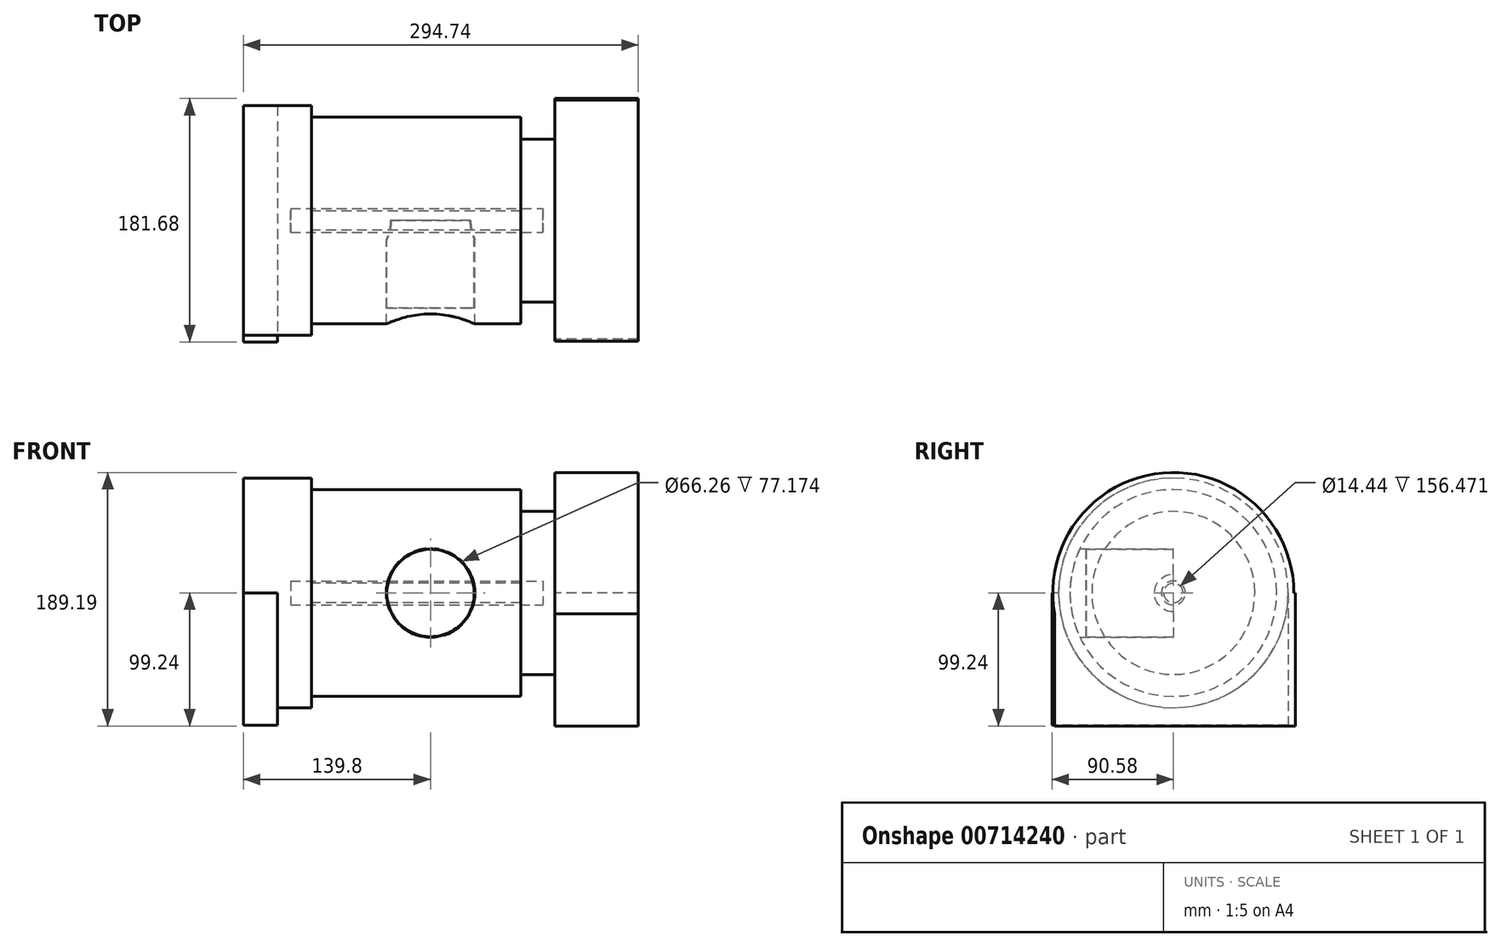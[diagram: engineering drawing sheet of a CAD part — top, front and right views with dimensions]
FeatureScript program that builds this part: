
annotation { "Feature Type Name" : "Feature", "Feature Type Description" : "" }
export const myFeature = defineFeature(function(context is Context, id is Id, definition is map)
    precondition{}
    {
        {
            var Q0;
            Q0=qCreatedBy(makeId("Front.planeOp"),FACE);
            var sketch = newSketch(context, id + "F0", { "sketchPlane" : qUnion([Q0])});
            skLineSegment(sketch, "E0.bottom", {"start": v(76.5, -43.24) * mm, "end": v(-76.5, -43.24) * mm});
            skLineSegment(sketch, "E0.top", {"start": v(76.5, 43.24) * mm, "end": v(-76.5, 43.24) * mm});
            skLineSegment(sketch, "E0.left", {"start": v(76.5, -43.24) * mm, "end": v(76.5, 43.24) * mm});
            skLineSegment(sketch, "E0.right", {"start": v(-76.5, -43.24) * mm, "end": v(-76.5, 43.24) * mm});
            skPoint(sketch, "E0.middle", {"position": v(0, 0) * mm});
            skSolve(sketch);
        }
        {
            var Q0;
            Q0=qCreatedBy(makeId("Right.planeOp"),FACE);
            var sketch = newSketch(context, id + "F1", { "sketchPlane" : qUnion([Q0])});
            skCircle(sketch, "E1", {"center": v(0, 0) * mm, "radius": 77.17 * mm});
            skSolve(sketch);
        }
        {
            var Q0;
            Q0=makeQuery(id+"F1.imprint","IMPRINT",FACE,{"disambiguationData":[TD([[makeQuery(id+"F1.imprint","IMPRINT",EDGE,{"derivedFrom":sQuery(id+"F1.wireOp",EDGE,"E1")}),1.0]])]});
            extrude(context, id + "F2", {"entities" : qUnion([Q0]), "oppositeDirection" : true, "depth" : 63.6 * mm, "offsetDistance" : 25.4 * mm, "hasSecondDirection" : true, "secondDirectionOppositeDirection" : false, "secondDirectionDepth" : 71.9 * mm});
        }
        {
            var Q0;
            Q0=makeQuery(id+"F2.opExtrude","CAP_FACE",FACE,{"disambiguationData":[OSD([sQuery(id+"F1.wireOp",EDGE,"E1")])],"isStart":true});
            var sketch = newSketch(context, id + "F3", { "sketchPlane" : qUnion([Q0])});
            skSolve(sketch);
        }
        {
            var Q0;
            Q0=makeQuery(id+"F3.imprint","IMPRINT",FACE,{"disambiguationData":[TD([[makeQuery(id+"F3.imprint","IMPRINT",EDGE,{"derivedFrom":makeQuery(id+"F2.opExtrude","CAP_EDGE",EDGE,{"disambiguationData":[OSD([sQuery(id+"F1.wireOp",EDGE,"E1")])],"isStart":true})}),1.0]])]});
            extrude(context, id + "F4", {"entities" : qUnion([Q0]), "operationType" : NewBodyOperationType.REMOVE, "oppositeDirection" : true, "depth" : 4.44 * mm, "offsetDistance" : 25.4 * mm});
        }
        {
            var Q0;
            Q0 = qSketchRegion(id + "F0", true);
            var sketch = newSketch(context, id + "F5", { "sketchPlane" : qUnion([Q0])});
            skCircle(sketch, "E2", {"center": v(0, 0) * mm, "radius": 33.13 * mm});
            skSolve(sketch);
        }
        {
            var Q0;
            Q0 = qSketchRegion(id + "F5", true);
            extrude(context, id + "F6", {"entities" : qUnion([Q0]), "operationType" : NewBodyOperationType.REMOVE, "depth" : 189.18 * mm, "offsetDistance" : 25.4 * mm});
        }
        {
            var Q0;
            Q0=makeQuery(id+"F0.imprint","IMPRINT",FACE,{"disambiguationData":[TD([[makeQuery(id+"F0.imprint","IMPRINT",EDGE,{"derivedFrom":sQuery(id+"F0.wireOp",EDGE,"E0.bottom")}),-1.0]])]});
            var sketch = newSketch(context, id + "F7", { "sketchPlane" : qUnion([Q0])});
            skCircle(sketch, "E3", {"center": v(0, 0) * mm, "radius": 32.56 * mm});
            skSolve(sketch);
        }
        {
            var Q0;
            Q0 = qSketchRegion(id + "F7", true);
            extrude(context, id + "F8", {"entities" : qUnion([Q0]), "depth" : 65.27 * mm, "offsetDistance" : 25.4 * mm});
        }
        {
            var Q0;
            Q0=makeQuery(id+"F2.opExtrude","CAP_FACE",FACE,{"disambiguationData":[OSD([sQuery(id+"F1.wireOp",EDGE,"E1")])],"isStart":false});
            var sketch = newSketch(context, id + "F9", { "sketchPlane" : qUnion([Q0])});
            skCircle(sketch, "E4", {"center": v(0, 0) * mm, "radius": 7.22 * mm});
            skSolve(sketch);
        }
        {
            var Q0;
            Q0=makeQuery(id+"F9.imprint","IMPRINT",FACE,{"disambiguationData":[TD([[makeQuery(id+"F9.imprint","IMPRINT",EDGE,{"derivedFrom":sQuery(id+"F9.wireOp",EDGE,"E4")}),1.0]])]});
            extrude(context, id + "F10", {"entities" : qUnion([Q0]), "operationType" : NewBodyOperationType.REMOVE, "oppositeDirection" : true, "depth" : 260.35 * mm, "offsetDistance" : 25.4 * mm});
        }
        {
            var Q0;
            Q0=makeQuery(id+"F2.opExtrude","CAP_FACE",FACE,{"disambiguationData":[OSD([sQuery(id+"F1.wireOp",EDGE,"E1")])],"isStart":false});
            var sketch = newSketch(context, id + "F11", { "sketchPlane" : qUnion([Q0])});
            skCircle(sketch, "E5", {"center": v(0, 0) * mm, "radius": 6.55 * mm});
            skSolve(sketch);
        }
        {
            var Q0;
            Q0=makeQuery(id+"F11.imprint","IMPRINT",FACE,{"disambiguationData":[TD([[makeQuery(id+"F11.imprint","IMPRINT",EDGE,{"derivedFrom":sQuery(id+"F11.wireOp",EDGE,"E5")}),-1.0]])]});
            extrude(context, id + "F12", {"entities" : qUnion([Q0]), "operationType" : NewBodyOperationType.REMOVE, "oppositeDirection" : true, "depth" : 115.25 * mm, "offsetDistance" : 25.4 * mm});
        }
        {
            var Q0;
            Q0=makeQuery(id+"F2.opExtrude","CAP_FACE",FACE,{"disambiguationData":[OSD([sQuery(id+"F1.wireOp",EDGE,"E1")])],"isStart":false});
            var sketch = newSketch(context, id + "F13", { "sketchPlane" : qUnion([Q0])});
            skCircle(sketch, "E6", {"center": v(0, 0) * mm, "radius": 14.1 * mm});
            skSolve(sketch);
        }
        {
            var Q0;
            Q0=makeQuery(id+"F13.imprint","IMPRINT",FACE,{"disambiguationData":[TD([[makeQuery(id+"F13.imprint","IMPRINT",EDGE,{"derivedFrom":sQuery(id+"F13.wireOp",EDGE,"E6")}),1.0]])]});
            extrude(context, id + "F14", {"entities" : qUnion([Q0]), "operationType" : NewBodyOperationType.ADD, "oppositeDirection" : true, "depth" : 172.6 * mm, "offsetDistance" : 25.4 * mm});
        }
        {
            var Q0;
            Q0=makeQuery(id+"F2.opExtrude","CAP_FACE",FACE,{"disambiguationData":[OSD([sQuery(id+"F1.wireOp",EDGE,"E1")])],"isStart":false});
            extrude(context, id + "F15", {"entities" : qUnion([Q0]), "operationType" : NewBodyOperationType.ADD, "depth" : 25.4 * mm, "offsetDistance" : 25.4 * mm});
        }
        {
            var Q0;
            Q0=makeQuery(id+"F15.opExtrude","CAP_FACE",FACE,{"disambiguationData":[OSD([sQuery(id+"F1.wireOp",EDGE,"E1")])],"isStart":false});
            var sketch = newSketch(context, id + "F16", { "sketchPlane" : qUnion([Q0])});
            skCircle(sketch, "E7", {"center": v(0, 0) * mm, "radius": 8.91 * mm});
            skSolve(sketch);
        }
        {
            var Q0;
            Q0 = qSketchRegion(id + "F16", true);
            extrude(context, id + "F17", {"entities" : qUnion([Q0]), "depth" : 15.58 * mm, "offsetDistance" : 25.4 * mm, "hasSecondDirection" : true, "secondDirectionOppositeDirection" : true, "secondDirectionDepth" : 172.93 * mm});
        }
        {
            var Q0;
            Q0=makeQuery(id+"F4.boolean.opBoolean","COPY",FACE,{"derivedFrom":makeQuery(id+"F4.opExtrude","CAP_FACE",FACE,{"disambiguationData":[OSD([sQuery(id+"F1.wireOp",EDGE,"E1")])],"isStart":false})});
            var sketch = newSketch(context, id + "F18", { "sketchPlane" : qUnion([Q0])});
            skCircle(sketch, "E8", {"center": v(0, 0) * mm, "radius": 60.82 * mm});
            skSolve(sketch);
        }
        {
            var Q0;
            Q0 = qSketchRegion(id + "F18", true);
            extrude(context, id + "F19", {"entities" : qUnion([Q0]), "depth" : 25.4 * mm, "offsetDistance" : 25.4 * mm});
        }
        {
            var Q0;
            Q0=makeQuery(id+"F15.opExtrude","CAP_FACE",FACE,{"disambiguationData":[OSD([sQuery(id+"F1.wireOp",EDGE,"E1")])],"isStart":false});
            var sketch = newSketch(context, id + "F20", { "sketchPlane" : qUnion([Q0])});
            skCircle(sketch, "E9", {"center": v(0, 0) * mm, "radius": 85.72 * mm});
            skSolve(sketch);
        }
        {
            var Q0;
            Q0 = qSketchRegion(id + "F20", true);
            extrude(context, id + "F21", {"entities" : qUnion([Q0]), "depth" : 25.4 * mm, "offsetDistance" : 25.4 * mm});
        }
        {
            var Q0;
            Q0=makeQuery(id+"F19.opExtrude","CAP_FACE",FACE,{"disambiguationData":[OSD([sQuery(id+"F18.wireOp",EDGE,"E8")])],"isStart":false});
            var sketch = newSketch(context, id + "F22", { "sketchPlane" : qUnion([Q0])});
            skCircle(sketch, "E10", {"center": v(0, 0) * mm, "radius": 79.55 * mm});
            skSolve(sketch);
        }
        {
            var Q0;
            Q0=makeQuery(id+"F19.opExtrude","CAP_FACE",FACE,{"disambiguationData":[OSD([sQuery(id+"F18.wireOp",EDGE,"E8")])],"isStart":false});
            var sketch = newSketch(context, id + "F23", { "sketchPlane" : qUnion([Q0])});
            skCircle(sketch, "E11", {"center": v(0, 0) * mm, "radius": 89.95 * mm});
            skSolve(sketch);
        }
        {
            var Q0;
            Q0 = qSketchRegion(id + "F23", true);
            var sketch = newSketch(context, id + "F24", { "sketchPlane" : qUnion([Q0])});
            skLineSegment(sketch, "E12.bottom", {"start": v(-88.57, 0) * mm, "end": v(91.1, 0) * mm});
            skLineSegment(sketch, "E12.top", {"start": v(-88.57, -99.24) * mm, "end": v(91.1, -99.24) * mm});
            skLineSegment(sketch, "E12.left", {"start": v(-88.57, 0) * mm, "end": v(-88.57, -99.24) * mm});
            skLineSegment(sketch, "E12.right", {"start": v(91.1, 0) * mm, "end": v(91.1, -99.24) * mm});
            skSolve(sketch);
        }
        {
            var Q0;
            {var subQ2=sQuery(id+"F24.wireOp",EDGE,"E12.top");Q0=makeQuery(id+"F24.imprint","IMPRINT",FACE,{"disambiguationData":[TD([[makeQuery(id+"F24.imprint","IMPRINT",EDGE,{"derivedFrom":subQ2}),1.0]])]});}
            var Q1;
            {var subQ0=sQuery(id+"F24.wireOp",EDGE,"E12.bottom");var subQ3=sQuery(id+"F24.wireOp",EDGE,"E12.left");var subQ7=makeQuery(id+"F24.imprint","INTERSECT",VERTEX,{"derivedFrom":[subQ0,subQ3]});Q1=makeQuery(id+"F24.imprint","IMPRINT",FACE,{"disambiguationData":[TD([[makeQuery(id+"F24.imprint","IMPRINT",EDGE,{"disambiguationData":[TD([[subQ7,-1.0]])],"derivedFrom":subQ0}),1.0]])]});}
            var Q2;
            Q2=makeQuery(id+"F23.imprint","IMPRINT",FACE,{"disambiguationData":[TD([[makeQuery(id+"F23.imprint","IMPRINT",EDGE,{"derivedFrom":makeQuery(id+"F19.opExtrude","CAP_EDGE",EDGE,{"disambiguationData":[OSD([sQuery(id+"F18.wireOp",EDGE,"E8")])],"isStart":false})}),1.0]])]});
            var Q3;
            {var subQ0=sQuery(id+"F24.wireOp",EDGE,"E12.bottom");var subQ3=sQuery(id+"F24.wireOp",EDGE,"E12.left");var subQ7=makeQuery(id+"F24.imprint","INTERSECT",VERTEX,{"derivedFrom":[subQ0,subQ3]});Q3=makeQuery(id+"F24.imprint","IMPRINT",FACE,{"disambiguationData":[TD([[makeQuery(id+"F24.imprint","IMPRINT",EDGE,{"disambiguationData":[TD([[subQ7,-1.0]])],"derivedFrom":subQ0}),-1.0]])]});}
            var Q4;
            Q4=sQuery(id+"F24.wireOp",EDGE,"E12.top");
            var Q5;
            Q5=sQuery(id+"F24.wireOp",EDGE,"E12.right");
            var Q6;
            Q6=sQuery(id+"F24.wireOp",EDGE,"E12.left");
            var Q7;
            Q7=sQuery(id+"F23.wireOp",EDGE,"E11");
            var Q8;
            Q8=sQuery(id+"F24.wireOp",EDGE,"E12.bottom");
            extrude(context, id + "F25", {"entities" : qUnion([Q0, Q1, Q2, Q3]), "operationType" : NewBodyOperationType.ADD, "surfaceEntities" : qUnion([Q4, Q5, Q6, Q7, Q8]), "depth" : 62.07 * mm, "offsetDistance" : 25.4 * mm});
        }
        {
            var Q0;
            Q0=makeQuery(id+"F21.opExtrude","CAP_FACE",FACE,{"disambiguationData":[OSD([sQuery(id+"F20.wireOp",EDGE,"E9")])],"isStart":false});
            var sketch = newSketch(context, id + "F26", { "sketchPlane" : qUnion([Q0])});
            skLineSegment(sketch, "E13.bottom", {"start": v(-85.72, 0) * mm, "end": v(90.58, 0) * mm});
            skLineSegment(sketch, "E13.top", {"start": v(-85.72, -98.65) * mm, "end": v(90.58, -98.65) * mm});
            skLineSegment(sketch, "E13.left", {"start": v(-85.72, 0) * mm, "end": v(-85.72, -98.65) * mm});
            skLineSegment(sketch, "E13.right", {"start": v(90.58, 0) * mm, "end": v(90.58, -98.65) * mm});
            skSolve(sketch);
        }
        {
            var Q0;
            {var subQ0=sQuery(id+"F26.wireOp",EDGE,"E13.bottom");var subQ1=makeQuery(id+"F21.opExtrude","CAP_EDGE",EDGE,{"disambiguationData":[OSD([sQuery(id+"F20.wireOp",EDGE,"E9")])],"isStart":false});var subQ3=makeQuery(id+"F26.imprint","INTERSECT",VERTEX,{"derivedFrom":[subQ1,subQ0]});Q0=makeQuery(id+"F26.imprint","IMPRINT",FACE,{"disambiguationData":[TD([[makeQuery(id+"F26.imprint","IMPRINT",EDGE,{"disambiguationData":[TD([[subQ3,1.0]])],"derivedFrom":subQ0}),1.0]])]});}
            var Q1;
            Q1=makeQuery(id+"F26.imprint","IMPRINT",FACE,{"disambiguationData":[TD([[makeQuery(id+"F26.imprint","IMPRINT",EDGE,{"derivedFrom":sQuery(id+"F26.wireOp",EDGE,"E13.top")}),1.0]])]});
            var Q2;
            {var subQ0=sQuery(id+"F26.wireOp",EDGE,"E13.bottom");var subQ1=makeQuery(id+"F21.opExtrude","CAP_EDGE",EDGE,{"disambiguationData":[OSD([sQuery(id+"F20.wireOp",EDGE,"E9")])],"isStart":false});var subQ3=makeQuery(id+"F26.imprint","INTERSECT",VERTEX,{"derivedFrom":[subQ1,subQ0]});Q2=makeQuery(id+"F26.imprint","IMPRINT",FACE,{"disambiguationData":[TD([[makeQuery(id+"F26.imprint","IMPRINT",EDGE,{"disambiguationData":[TD([[subQ3,1.0]])],"derivedFrom":subQ0}),-1.0]])]});}
            var Q3;
            Q3=sQuery(id+"F26.wireOp",EDGE,"E13.right");
            var Q4;
            Q4=sQuery(id+"F26.wireOp",EDGE,"E13.top");
            var Q5;
            Q5=sQuery(id+"F26.wireOp",EDGE,"E13.left");
            var Q6;
            Q6=sQuery(id+"F26.wireOp",EDGE,"E13.bottom");
            extrude(context, id + "F27", {"entities" : qUnion([Q0, Q1, Q2]), "operationType" : NewBodyOperationType.ADD, "surfaceEntities" : qUnion([Q3, Q4, Q5, Q6]), "depth" : 25.4 * mm, "offsetDistance" : 25.4 * mm});
        }
    });
